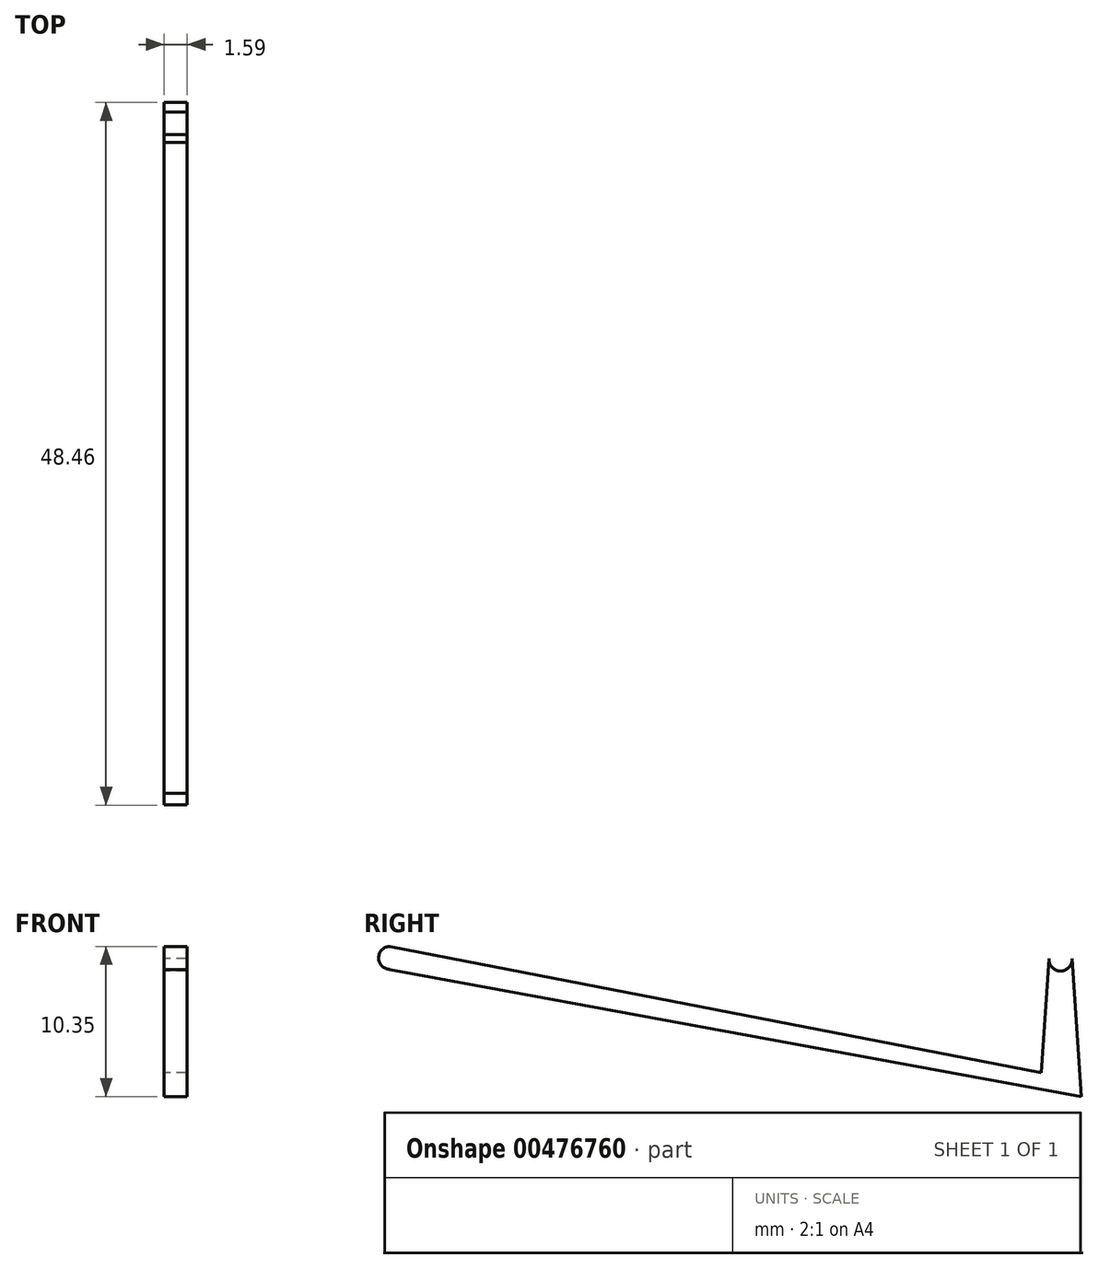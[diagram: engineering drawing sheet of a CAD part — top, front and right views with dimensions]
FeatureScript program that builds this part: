
annotation { "Feature Type Name" : "Feature", "Feature Type Description" : "" }
export const myFeature = defineFeature(function(context is Context, id is Id, definition is map)
    precondition{}
    {
        {
            var Q0;
            Q0=qCreatedBy(makeId("Right.planeOp"),FACE);
            var sketch = newSketch(context, id + "F0", { "sketchPlane" : qUnion([Q0])});
            skLineSegment(sketch, "E0.right", {"start": v(-23.13, -0.74) * mm, "end": v(-23.1, 0.85) * mm});
            skPoint(sketch, "E0.middle", {"position": v(0, 0) * mm});
            skCircle(sketch, "E1", {"center": v(-23.11, 0.05) * mm, "radius": 0.8 * mm});
            skCircle(sketch, "E2", {"center": v(23.11, -0.05) * mm, "radius": 0.8 * mm});
            skLineSegment(sketch, "E3", {"start": v(22.32, 0) * mm, "end": v(21.79, -7.86) * mm});
            skLineSegment(sketch, "E4", {"start": v(23.9, 0) * mm, "end": v(24.55, -9.5) * mm});
            skLineSegment(sketch, "E5", {"start": v(24.55, -9.5) * mm, "end": v(-23.13, -0.74) * mm});
            skLineSegment(sketch, "E6", {"start": v(21.79, -7.86) * mm, "end": v(-23.1, 0.85) * mm});
            skPoint(sketch, "E7.orphan", {"position": v(23.13, 0.74) * mm});
            skPoint(sketch, "E0.left.start.orphan", {"position": v(23.1, -0.85) * mm});
            skSolve(sketch);
        }
        {
            var Q0;
            {var subQ0=sQuery(id+"F0.wireOp",EDGE,"E0.left");Q0=makeQuery(id+"F0.imprint","IMPRINT",FACE,{"disambiguationData":[TD([[makeQuery(id+"F0.imprint","IMPRINT",EDGE,{"derivedFrom":subQ0}),-1.0]])]});}
            var Q1;
            {var subQ0=sQuery(id+"F0.wireOp",EDGE,"E0.left");Q1=makeQuery(id+"F0.imprint","IMPRINT",FACE,{"disambiguationData":[TD([[makeQuery(id+"F0.imprint","IMPRINT",EDGE,{"derivedFrom":subQ0}),1.0]])]});}
            var Q2;
            {var subQ3=sQuery(id+"F0.wireOp",EDGE,"E3");Q2=makeQuery(id+"F0.imprint","IMPRINT",FACE,{"disambiguationData":[TD([[makeQuery(id+"F0.imprint","IMPRINT",EDGE,{"derivedFrom":subQ3}),1.0]])]});}
            var Q3;
            {var subQ0=sQuery(id+"F0.wireOp",EDGE,"E0.right");Q3=makeQuery(id+"F0.imprint","IMPRINT",FACE,{"disambiguationData":[TD([[makeQuery(id+"F0.imprint","IMPRINT",EDGE,{"derivedFrom":subQ0}),-1.0]])]});}
            var Q4;
            {var subQ0=sQuery(id+"F0.wireOp",EDGE,"E0.right");Q4=makeQuery(id+"F0.imprint","IMPRINT",FACE,{"disambiguationData":[TD([[makeQuery(id+"F0.imprint","IMPRINT",EDGE,{"derivedFrom":subQ0}),1.0]])]});}
            extrude(context, id + "F1", {"entities" : qUnion([Q0, Q1, Q2, Q3, Q4]), "depth" : 1.59 * mm});
        }
    });
